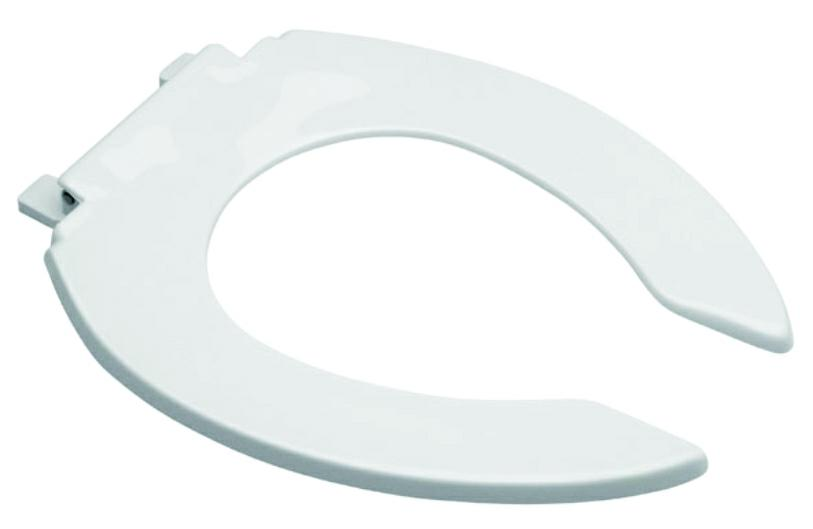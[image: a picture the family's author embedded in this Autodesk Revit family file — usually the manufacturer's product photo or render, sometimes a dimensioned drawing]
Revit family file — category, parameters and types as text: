
# Revit family: Asiento AF-1
name_source: partatom
category: Aparatos sanitarios
revit_build: Autodesk Revit 2016 (Build: 20150220_1215(x64)
units: mm (PartAtom-declared; Revit-internal decimal feet)

## family parameters
Compartido = Sí
Corte con vacíos al cargar = No
Cota de conector redondo = Diámetro de uso
Número OmniClass = 23.45.00.00
Punto de cálculo de habitación = Sí
Se basa en plano de trabajo = No
Siempre vertical = Sí
Tipo de pieza = Normal
Título OmniClass = Sanitary, Laundry, and Cleaning Equipment

## types (1)
- AF-1
    Comentarios de tipo = SANIVEX
    Data Sheet = http://www.helvex.com.mx
    Descripción = Seat Without Lid Elongated Front Plus Open For Antibacterial Flush Valve Cup, White
    Fabricante = HELVEX
    Features = Glossy Finish; Antibacterial Protection
    Imagen de tipo = AF-1.jpg
    Modelo = AF-1
    Placement Height = 14.5" And 17"
    Polypropylene = Polypropylene
    Total Height = 1"
    Total Length = 19"
    Total Weight = 1.54 lb
    Total Width = 14"
    URL = http://www.helvex.com.mx

## geometry (parser evidence)
native form markers: Sweep x3
no freeform markers — native parametric forms only
